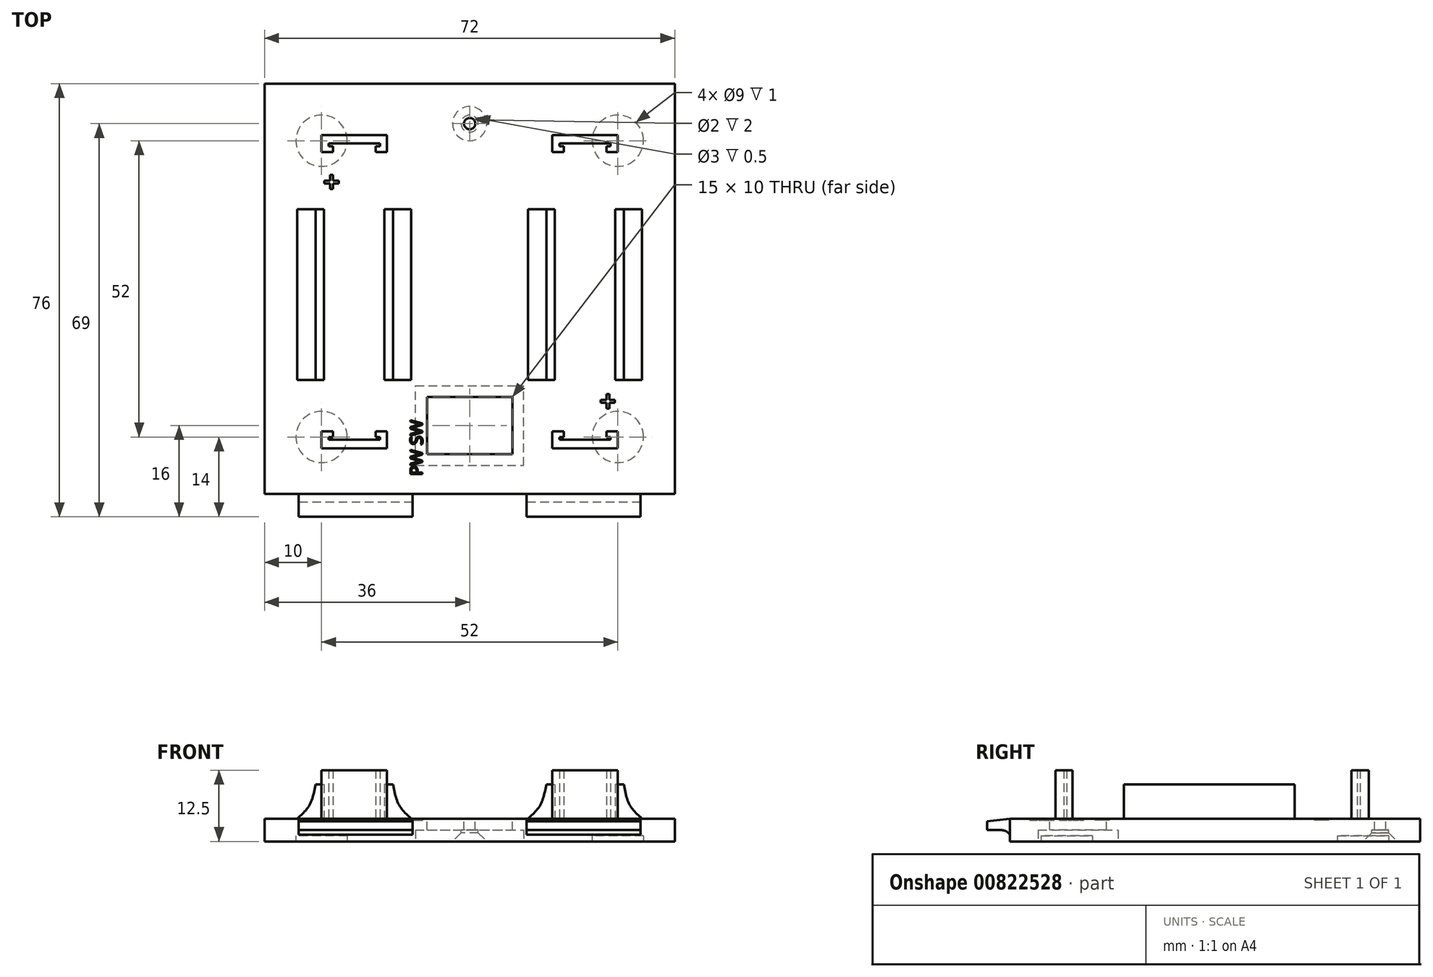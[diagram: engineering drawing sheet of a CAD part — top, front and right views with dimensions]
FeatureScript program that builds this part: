
annotation { "Feature Type Name" : "Feature", "Feature Type Description" : "" }
export const myFeature = defineFeature(function(context is Context, id is Id, definition is map)
    precondition{}
    {
        {
            var Q0;
            Q0=qCreatedBy(makeId("Top.planeOp"),FACE);
            var sketch = newSketch(context, id + "F0", { "sketchPlane" : qUnion([Q0])});
            skLineSegment(sketch, "E0.bottom", {"start": v(-36, 36) * mm, "end": v(36, 36) * mm});
            skLineSegment(sketch, "E0.top", {"start": v(-36, -36) * mm, "end": v(36, -36) * mm});
            skLineSegment(sketch, "E0.left", {"start": v(-36, 36) * mm, "end": v(-36, -36) * mm});
            skLineSegment(sketch, "E0.right", {"start": v(36, 36) * mm, "end": v(36, -36) * mm});
            skLineSegment(sketch, "E1.bottom", {"start": v(-36, -36) * mm, "end": v(-16, -36) * mm});
            skLineSegment(sketch, "E1.top", {"start": v(-36, -40) * mm, "end": v(-16, -40) * mm});
            skLineSegment(sketch, "E1.left", {"start": v(-36, -36) * mm, "end": v(-36, -40) * mm});
            skLineSegment(sketch, "E1.right", {"start": v(-16, -36) * mm, "end": v(-16, -40) * mm});
            skLineSegment(sketch, "E2.bottom", {"start": v(16, -36) * mm, "end": v(36, -36) * mm});
            skLineSegment(sketch, "E2.top", {"start": v(16, -40) * mm, "end": v(36, -40) * mm});
            skLineSegment(sketch, "E2.left", {"start": v(16, -36) * mm, "end": v(16, -40) * mm});
            skLineSegment(sketch, "E2.right", {"start": v(36, -36) * mm, "end": v(36, -40) * mm});
            skLineSegment(sketch, "E3", {"start": v(-16, -40) * mm, "end": v(16, -40) * mm});
            skLineSegment(sketch, "E4", {"start": v(-16, -36) * mm, "end": v(16, -36) * mm});
            skLineSegment(sketch, "E5", {"start": v(-10, -40) * mm, "end": v(-10, -36) * mm});
            skLineSegment(sketch, "E6", {"start": v(10, -40) * mm, "end": v(10, -36) * mm});
            skPoint(sketch, "E6.endSnap0", {"position": v(0, -36) * mm});
            skSolve(sketch);
        }
        {
            var Q0;
            Q0=makeQuery(id+"F0.imprint","IMPRINT",FACE,{"disambiguationData":[TD([[makeQuery(id+"F0.imprint","IMPRINT",EDGE,{"derivedFrom":sQuery(id+"F0.wireOp",EDGE,"E0.bottom")}),-1.0]])]});
            extrude(context, id + "F1", {"entities" : qUnion([Q0]), "depth" : 4 * mm, "offsetDistance" : 25 * mm});
        }
        {
            var Q0;
            Q0=makeQuery(id+"F1.opExtrude","CAP_FACE",FACE,{"disambiguationData":[OSD([sQuery(id+"F0.wireOp",EDGE,"E0.bottom"),sQuery(id+"F0.wireOp",EDGE,"E0.top"),sQuery(id+"F0.wireOp",EDGE,"E0.left"),sQuery(id+"F0.wireOp",EDGE,"E0.right")])],"isStart":false});
            var sketch = newSketch(context, id + "F2", { "sketchPlane" : qUnion([Q0])});
            skLineSegment(sketch, "E7.bottom", {"start": v(-26, 27) * mm, "end": v(-24, 27) * mm});
            skLineSegment(sketch, "E7.top", {"start": v(-26, 24) * mm, "end": v(-24, 24) * mm});
            skLineSegment(sketch, "E7.left", {"start": v(-26, 27) * mm, "end": v(-26, 24) * mm});
            skLineSegment(sketch, "E7.right", {"start": v(-24, 27) * mm, "end": v(-24, 24) * mm});
            skLineSegment(sketch, "E8.bottom", {"start": v(-16.5, 27) * mm, "end": v(-14.5, 27) * mm});
            skLineSegment(sketch, "E8.top", {"start": v(-16.5, 24) * mm, "end": v(-14.5, 24) * mm});
            skLineSegment(sketch, "E8.left", {"start": v(-16.5, 27) * mm, "end": v(-16.5, 24) * mm});
            skLineSegment(sketch, "E8.right", {"start": v(-14.5, 27) * mm, "end": v(-14.5, 24) * mm});
            skLineSegment(sketch, "E9", {"start": v(-24, 27) * mm, "end": v(-16.5, 27) * mm});
            skLineSegment(sketch, "E10", {"start": v(-24, 25) * mm, "end": v(-16.5, 25) * mm, "construction": true});
            skLineSegment(sketch, "E11", {"start": v(-24, 25.5) * mm, "end": v(-16.5, 25.5) * mm});
            skLineSegment(sketch, "E12", {"start": v(-24, 25.5) * mm, "end": v(-24.75, 25.5) * mm});
            skLineSegment(sketch, "E13", {"start": v(-24.75, 25.5) * mm, "end": v(-24.75, 25) * mm});
            skLineSegment(sketch, "E14", {"start": v(-24.75, 25) * mm, "end": v(-24, 25) * mm});
            skLineSegment(sketch, "E15", {"start": v(-16.5, 25.5) * mm, "end": v(-15.75, 25.5) * mm});
            skLineSegment(sketch, "E16", {"start": v(-15.75, 25.5) * mm, "end": v(-15.75, 25) * mm});
            skLineSegment(sketch, "E17", {"start": v(-15.75, 25) * mm, "end": v(-16.5, 25) * mm});
            skLineSegment(sketch, "E18.bottom", {"start": v(-14.5, -28) * mm, "end": v(-16.5, -28) * mm});
            skLineSegment(sketch, "E18.top", {"start": v(-14.5, -25) * mm, "end": v(-16.5, -25) * mm});
            skLineSegment(sketch, "E18.left", {"start": v(-14.5, -28) * mm, "end": v(-14.5, -25) * mm});
            skLineSegment(sketch, "E18.right", {"start": v(-16.5, -28) * mm, "end": v(-16.5, -25) * mm});
            skLineSegment(sketch, "E19.bottom", {"start": v(-24, -28) * mm, "end": v(-26, -28) * mm});
            skLineSegment(sketch, "E19.top", {"start": v(-24, -25) * mm, "end": v(-26, -25) * mm});
            skLineSegment(sketch, "E19.left", {"start": v(-24, -28) * mm, "end": v(-24, -25) * mm});
            skLineSegment(sketch, "E19.right", {"start": v(-26, -28) * mm, "end": v(-26, -25) * mm});
            skLineSegment(sketch, "E20", {"start": v(-16.5, -28) * mm, "end": v(-24, -28) * mm});
            skLineSegment(sketch, "E21", {"start": v(-16.5, -26) * mm, "end": v(-24, -26) * mm, "construction": true});
            skLineSegment(sketch, "E22", {"start": v(-16.5, -26.5) * mm, "end": v(-24, -26.5) * mm});
            skLineSegment(sketch, "E23", {"start": v(-16.5, -26.5) * mm, "end": v(-15.75, -26.5) * mm});
            skLineSegment(sketch, "E24", {"start": v(-15.75, -26.5) * mm, "end": v(-15.75, -26) * mm});
            skLineSegment(sketch, "E25", {"start": v(-15.75, -26) * mm, "end": v(-16.5, -26) * mm});
            skLineSegment(sketch, "E26", {"start": v(-24, -26.5) * mm, "end": v(-24.75, -26.5) * mm});
            skLineSegment(sketch, "E27", {"start": v(-24.75, -26.5) * mm, "end": v(-24.75, -26) * mm});
            skLineSegment(sketch, "E28", {"start": v(-24.75, -26) * mm, "end": v(-24, -26) * mm});
            skLineSegment(sketch, "E29.bottom", {"start": v(14.5, 27) * mm, "end": v(16.5, 27) * mm});
            skLineSegment(sketch, "E29.top", {"start": v(14.5, 24) * mm, "end": v(16.5, 24) * mm});
            skLineSegment(sketch, "E29.left", {"start": v(14.5, 27) * mm, "end": v(14.5, 24) * mm});
            skLineSegment(sketch, "E29.right", {"start": v(16.5, 27) * mm, "end": v(16.5, 24) * mm});
            skLineSegment(sketch, "E30.bottom", {"start": v(24, 27) * mm, "end": v(26, 27) * mm});
            skLineSegment(sketch, "E30.top", {"start": v(24, 24) * mm, "end": v(26, 24) * mm});
            skLineSegment(sketch, "E30.left", {"start": v(24, 27) * mm, "end": v(24, 24) * mm});
            skLineSegment(sketch, "E30.right", {"start": v(26, 27) * mm, "end": v(26, 24) * mm});
            skLineSegment(sketch, "E31", {"start": v(16.5, 27) * mm, "end": v(24, 27) * mm});
            skLineSegment(sketch, "E32", {"start": v(16.5, 25) * mm, "end": v(24, 25) * mm, "construction": true});
            skLineSegment(sketch, "E33", {"start": v(16.5, 25.5) * mm, "end": v(24, 25.5) * mm});
            skLineSegment(sketch, "E34", {"start": v(16.5, 25.5) * mm, "end": v(15.75, 25.5) * mm});
            skLineSegment(sketch, "E35", {"start": v(15.75, 25.5) * mm, "end": v(15.75, 25) * mm});
            skLineSegment(sketch, "E36", {"start": v(15.75, 25) * mm, "end": v(16.5, 25) * mm});
            skLineSegment(sketch, "E37", {"start": v(24, 25.5) * mm, "end": v(24.75, 25.5) * mm});
            skLineSegment(sketch, "E38", {"start": v(24.75, 25.5) * mm, "end": v(24.75, 25) * mm});
            skLineSegment(sketch, "E39", {"start": v(24.75, 25) * mm, "end": v(24, 25) * mm});
            skLineSegment(sketch, "E40.bottom", {"start": v(26, -28) * mm, "end": v(24, -28) * mm});
            skLineSegment(sketch, "E40.top", {"start": v(26, -25) * mm, "end": v(24, -25) * mm});
            skLineSegment(sketch, "E40.left", {"start": v(26, -28) * mm, "end": v(26, -25) * mm});
            skLineSegment(sketch, "E40.right", {"start": v(24, -28) * mm, "end": v(24, -25) * mm});
            skLineSegment(sketch, "E41.bottom", {"start": v(16.5, -28) * mm, "end": v(14.5, -28) * mm});
            skLineSegment(sketch, "E41.top", {"start": v(16.5, -25) * mm, "end": v(14.5, -25) * mm});
            skLineSegment(sketch, "E41.left", {"start": v(16.5, -28) * mm, "end": v(16.5, -25) * mm});
            skLineSegment(sketch, "E41.right", {"start": v(14.5, -28) * mm, "end": v(14.5, -25) * mm});
            skLineSegment(sketch, "E42", {"start": v(24, -28) * mm, "end": v(16.5, -28) * mm});
            skLineSegment(sketch, "E43", {"start": v(24, -26) * mm, "end": v(16.5, -26) * mm, "construction": true});
            skLineSegment(sketch, "E44", {"start": v(24, -26.5) * mm, "end": v(16.5, -26.5) * mm});
            skLineSegment(sketch, "E45", {"start": v(24, -26.5) * mm, "end": v(24.75, -26.5) * mm});
            skLineSegment(sketch, "E46", {"start": v(24.75, -26.5) * mm, "end": v(24.75, -26) * mm});
            skLineSegment(sketch, "E47", {"start": v(24.75, -26) * mm, "end": v(24, -26) * mm});
            skLineSegment(sketch, "E48", {"start": v(16.5, -26.5) * mm, "end": v(15.75, -26.5) * mm});
            skLineSegment(sketch, "E49", {"start": v(15.75, -26.5) * mm, "end": v(15.75, -26) * mm});
            skLineSegment(sketch, "E50", {"start": v(15.75, -26) * mm, "end": v(16.5, -26) * mm});
            skLineSegment(sketch, "E51", {"start": v(-14.5, 27) * mm, "end": v(14.5, 27) * mm, "construction": true});
            skLineSegment(sketch, "E52", {"start": v(-20.25, 25) * mm, "end": v(-20.25, -26) * mm, "construction": true});
            skLineSegment(sketch, "E53", {"start": v(20.25, 25) * mm, "end": v(20.25, -26) * mm, "construction": true});
            skLineSegment(sketch, "E54.bottom", {"start": v(-27.05, 14) * mm, "end": v(-25.55, 14) * mm});
            skLineSegment(sketch, "E54.top", {"start": v(-27.05, 4) * mm, "end": v(-25.55, 4) * mm});
            skLineSegment(sketch, "E54.left", {"start": v(-27.05, 14) * mm, "end": v(-27.05, 4) * mm});
            skLineSegment(sketch, "E54.right", {"start": v(-25.55, 14) * mm, "end": v(-25.55, 4) * mm});
            skLineSegment(sketch, "E55", {"start": v(-26, 24) * mm, "end": v(-42.81, 24) * mm, "construction": true});
            skLineSegment(sketch, "E56.bottom", {"start": v(-27.05, -6) * mm, "end": v(-25.55, -6) * mm});
            skLineSegment(sketch, "E56.top", {"start": v(-27.05, -16) * mm, "end": v(-25.55, -16) * mm});
            skLineSegment(sketch, "E56.left", {"start": v(-27.05, -6) * mm, "end": v(-27.05, -16) * mm});
            skLineSegment(sketch, "E56.right", {"start": v(-25.55, -6) * mm, "end": v(-25.55, -16) * mm});
            skLineSegment(sketch, "E57.MirrorCS", {"start": v(-14.95, 14) * mm, "end": v(-14.95, 4) * mm});
            skLineSegment(sketch, "E58.MirrorCS", {"start": v(-13.45, 14) * mm, "end": v(-13.45, 4) * mm});
            skLineSegment(sketch, "E59.MirrorCS", {"start": v(-13.45, 14) * mm, "end": v(-14.95, 14) * mm});
            skLineSegment(sketch, "E60.MirrorCS", {"start": v(-13.45, 4) * mm, "end": v(-14.95, 4) * mm});
            skLineSegment(sketch, "E61.MirrorCS", {"start": v(-14.95, -6) * mm, "end": v(-14.95, -16) * mm});
            skLineSegment(sketch, "E62.MirrorCS", {"start": v(-13.45, -6) * mm, "end": v(-13.45, -16) * mm});
            skLineSegment(sketch, "E63.MirrorCS", {"start": v(-13.45, -6) * mm, "end": v(-14.95, -6) * mm});
            skLineSegment(sketch, "E64.MirrorCS", {"start": v(-13.45, -16) * mm, "end": v(-14.95, -16) * mm});
            skLineSegment(sketch, "E65", {"start": v(14.5, 24) * mm, "end": v(3.37, 24) * mm, "construction": true});
            skLineSegment(sketch, "E66.bottom", {"start": v(13.45, 14) * mm, "end": v(14.95, 14) * mm});
            skLineSegment(sketch, "E66.top", {"start": v(13.45, 4) * mm, "end": v(14.95, 4) * mm});
            skLineSegment(sketch, "E66.left", {"start": v(13.45, 14) * mm, "end": v(13.45, 4) * mm});
            skLineSegment(sketch, "E66.right", {"start": v(14.95, 14) * mm, "end": v(14.95, 4) * mm});
            skLineSegment(sketch, "E67.bottom", {"start": v(13.45, -6) * mm, "end": v(14.95, -6) * mm});
            skLineSegment(sketch, "E67.top", {"start": v(13.45, -16) * mm, "end": v(14.95, -16) * mm});
            skLineSegment(sketch, "E67.left", {"start": v(13.45, -6) * mm, "end": v(13.45, -16) * mm});
            skLineSegment(sketch, "E67.right", {"start": v(14.95, -6) * mm, "end": v(14.95, -16) * mm});
            skLineSegment(sketch, "E68.MirrorCS", {"start": v(25.55, 14) * mm, "end": v(25.55, 4) * mm});
            skLineSegment(sketch, "E69.MirrorCS", {"start": v(27.05, 14) * mm, "end": v(27.05, 4) * mm});
            skLineSegment(sketch, "E70.MirrorCS", {"start": v(27.05, 4) * mm, "end": v(25.55, 4) * mm});
            skLineSegment(sketch, "E71.MirrorCS", {"start": v(27.05, 14) * mm, "end": v(25.55, 14) * mm});
            skLineSegment(sketch, "E72.MirrorCS", {"start": v(27.05, -6) * mm, "end": v(25.55, -6) * mm});
            skLineSegment(sketch, "E73.MirrorCS", {"start": v(25.55, -6) * mm, "end": v(25.55, -16) * mm});
            skLineSegment(sketch, "E74.MirrorCS", {"start": v(27.05, -6) * mm, "end": v(27.05, -16) * mm});
            skLineSegment(sketch, "E75.MirrorCS", {"start": v(27.05, -16) * mm, "end": v(25.55, -16) * mm});
            skLineSegment(sketch, "E76", {"start": v(-24, -25) * mm, "end": v(-16.5, -25) * mm, "construction": true});
            skLineSegment(sketch, "E77", {"start": v(16.5, -25) * mm, "end": v(24, -25) * mm, "construction": true});
            skLineSegment(sketch, "E78", {"start": v(16.5, 24) * mm, "end": v(24, 24) * mm, "construction": true});
            skLineSegment(sketch, "E79", {"start": v(-24, 24) * mm, "end": v(-16.5, 24) * mm, "construction": true});
            skLineSegment(sketch, "E80.bottom", {"start": v(-24.5, 20) * mm, "end": v(-24, 20) * mm});
            skLineSegment(sketch, "E80.top", {"start": v(-24.5, 17.5) * mm, "end": v(-24, 17.5) * mm});
            skLineSegment(sketch, "E80.left", {"start": v(-24.5, 20) * mm, "end": v(-24.5, 19) * mm});
            skLineSegment(sketch, "E80.right", {"start": v(-24, 20) * mm, "end": v(-24, 19) * mm});
            skLineSegment(sketch, "E81.bottom", {"start": v(-23, 19) * mm, "end": v(-24, 19) * mm});
            skLineSegment(sketch, "E81.top", {"start": v(-23, 18.5) * mm, "end": v(-24, 18.5) * mm});
            skLineSegment(sketch, "E81.left", {"start": v(-23, 19) * mm, "end": v(-23, 18.5) * mm});
            skLineSegment(sketch, "E81.right", {"start": v(-25.5, 19) * mm, "end": v(-25.5, 18.5) * mm});
            skLineSegment(sketch, "E82", {"start": v(-25.5, 18.75) * mm, "end": v(-23, 18.75) * mm, "construction": true});
            skLineSegment(sketch, "E83", {"start": v(-24.25, 20) * mm, "end": v(-24.25, 17.5) * mm, "construction": true});
            skLineSegment(sketch, "E84.trimOffspring", {"start": v(-24.5, 18.5) * mm, "end": v(-24.5, 17.5) * mm});
            skLineSegment(sketch, "E85.trimOffspring", {"start": v(-24.5, 18.5) * mm, "end": v(-25.5, 18.5) * mm});
            skLineSegment(sketch, "E86.trimOffspring", {"start": v(-24, 18.5) * mm, "end": v(-24, 17.5) * mm});
            skLineSegment(sketch, "E87.trimOffspring", {"start": v(-24.5, 19) * mm, "end": v(-25.5, 19) * mm});
            skLineSegment(sketch, "E88.bottom", {"start": v(24, -18.5) * mm, "end": v(24.5, -18.5) * mm});
            skLineSegment(sketch, "E88.top", {"start": v(24, -21) * mm, "end": v(24.5, -21) * mm});
            skLineSegment(sketch, "E88.left", {"start": v(24, -18.5) * mm, "end": v(24, -19.5) * mm});
            skLineSegment(sketch, "E88.right", {"start": v(24.5, -18.5) * mm, "end": v(24.5, -19.5) * mm});
            skLineSegment(sketch, "E89.bottom", {"start": v(25.5, -19.5) * mm, "end": v(24.5, -19.5) * mm});
            skLineSegment(sketch, "E89.top", {"start": v(25.5, -20) * mm, "end": v(24.5, -20) * mm});
            skLineSegment(sketch, "E89.left", {"start": v(25.5, -19.5) * mm, "end": v(25.5, -20) * mm});
            skLineSegment(sketch, "E89.right", {"start": v(23, -19.5) * mm, "end": v(23, -20) * mm});
            skLineSegment(sketch, "E90", {"start": v(23, -19.75) * mm, "end": v(25.5, -19.75) * mm, "construction": true});
            skLineSegment(sketch, "E91", {"start": v(24.25, -18.5) * mm, "end": v(24.25, -21) * mm, "construction": true});
            skLineSegment(sketch, "E92.trimOffspring", {"start": v(24, -20) * mm, "end": v(24, -21) * mm});
            skLineSegment(sketch, "E93.trimOffspring", {"start": v(24, -20) * mm, "end": v(23, -20) * mm});
            skLineSegment(sketch, "E94.trimOffspring", {"start": v(24.5, -20) * mm, "end": v(24.5, -21) * mm});
            skLineSegment(sketch, "E95.trimOffspring", {"start": v(24, -19.5) * mm, "end": v(23, -19.5) * mm});
            skLineSegment(sketch, "E96", {"start": v(-27.05, 4) * mm, "end": v(-27.05, -6) * mm});
            skLineSegment(sketch, "E97", {"start": v(-25.55, 4) * mm, "end": v(-25.55, -6) * mm});
            skLineSegment(sketch, "E98", {"start": v(-14.95, 4) * mm, "end": v(-14.95, -6) * mm});
            skLineSegment(sketch, "E99", {"start": v(-13.45, 4) * mm, "end": v(-13.45, -6) * mm});
            skLineSegment(sketch, "E100", {"start": v(25.55, 4) * mm, "end": v(25.55, -6) * mm});
            skLineSegment(sketch, "E101", {"start": v(27.05, 4) * mm, "end": v(27.05, -6) * mm});
            skLineSegment(sketch, "E102", {"start": v(13.45, 4) * mm, "end": v(13.45, -6) * mm});
            skLineSegment(sketch, "E103", {"start": v(14.95, 4) * mm, "end": v(14.95, -6) * mm});
            skSolve(sketch);
        }
        {
            var Q0;
            Q0=makeQuery(id+"F2.imprint","IMPRINT",FACE,{"disambiguationData":[TD([[makeQuery(id+"F2.imprint","IMPRINT",EDGE,{"derivedFrom":sQuery(id+"F2.wireOp",EDGE,"E56.bottom")}),-1.0]])]});
            var Q1;
            Q1=makeQuery(id+"F2.imprint","IMPRINT",FACE,{"disambiguationData":[TD([[makeQuery(id+"F2.imprint","IMPRINT",EDGE,{"derivedFrom":sQuery(id+"F2.wireOp",EDGE,"E61.MirrorCS")}),1.0]])]});
            var Q2;
            Q2=makeQuery(id+"F2.imprint","IMPRINT",FACE,{"disambiguationData":[TD([[makeQuery(id+"F2.imprint","IMPRINT",EDGE,{"derivedFrom":sQuery(id+"F2.wireOp",EDGE,"E57.MirrorCS")}),1.0]])]});
            var Q3;
            Q3=makeQuery(id+"F2.imprint","IMPRINT",FACE,{"disambiguationData":[TD([[makeQuery(id+"F2.imprint","IMPRINT",EDGE,{"derivedFrom":sQuery(id+"F2.wireOp",EDGE,"E54.bottom")}),-1.0]])]});
            var Q4;
            Q4=makeQuery(id+"F2.imprint","IMPRINT",FACE,{"disambiguationData":[TD([[makeQuery(id+"F2.imprint","IMPRINT",EDGE,{"derivedFrom":sQuery(id+"F2.wireOp",EDGE,"E67.bottom")}),-1.0]])]});
            var Q5;
            Q5=makeQuery(id+"F2.imprint","IMPRINT",FACE,{"disambiguationData":[TD([[makeQuery(id+"F2.imprint","IMPRINT",EDGE,{"derivedFrom":sQuery(id+"F2.wireOp",EDGE,"E66.bottom")}),-1.0]])]});
            var Q6;
            Q6=makeQuery(id+"F2.imprint","IMPRINT",FACE,{"disambiguationData":[TD([[makeQuery(id+"F2.imprint","IMPRINT",EDGE,{"derivedFrom":sQuery(id+"F2.wireOp",EDGE,"E68.MirrorCS")}),1.0]])]});
            var Q7;
            Q7=makeQuery(id+"F2.imprint","IMPRINT",FACE,{"disambiguationData":[TD([[makeQuery(id+"F2.imprint","IMPRINT",EDGE,{"derivedFrom":sQuery(id+"F2.wireOp",EDGE,"E72.MirrorCS")}),1.0]])]});
            var Q8;
            Q8=makeQuery(id+"F2.imprint","IMPRINT",FACE,{"disambiguationData":[TD([[makeQuery(id+"F2.imprint","IMPRINT",EDGE,{"derivedFrom":sQuery(id+"F2.wireOp",EDGE,"E54.top")}),-1.0]])]});
            var Q9;
            Q9=makeQuery(id+"F2.imprint","IMPRINT",FACE,{"disambiguationData":[TD([[makeQuery(id+"F2.imprint","IMPRINT",EDGE,{"derivedFrom":sQuery(id+"F2.wireOp",EDGE,"E60.MirrorCS")}),1.0]])]});
            var Q10;
            Q10=makeQuery(id+"F2.imprint","IMPRINT",FACE,{"disambiguationData":[TD([[makeQuery(id+"F2.imprint","IMPRINT",EDGE,{"derivedFrom":sQuery(id+"F2.wireOp",EDGE,"E66.top")}),-1.0]])]});
            var Q11;
            Q11=makeQuery(id+"F2.imprint","IMPRINT",FACE,{"disambiguationData":[TD([[makeQuery(id+"F2.imprint","IMPRINT",EDGE,{"derivedFrom":sQuery(id+"F2.wireOp",EDGE,"E70.MirrorCS")}),1.0]])]});
            extrude(context, id + "F3", {"entities" : qUnion([Q0, Q1, Q2, Q3, Q4, Q5, Q6, Q7, Q8, Q9, Q10, Q11]), "operationType" : NewBodyOperationType.ADD, "depth" : 6 * mm, "offsetDistance" : 25 * mm});
        }
        {
            var Q0;
            {var subQ1=sQuery(id+"F2.wireOp",EDGE,"E7.bottom");Q0=makeQuery(id+"F2.imprint","IMPRINT",FACE,{"disambiguationData":[TD([[makeQuery(id+"F2.imprint","IMPRINT",EDGE,{"derivedFrom":subQ1}),-1.0]])]});}
            var Q1;
            {var subQ0=sQuery(id+"F2.wireOp",EDGE,"E9");Q1=makeQuery(id+"F2.imprint","IMPRINT",FACE,{"disambiguationData":[TD([[makeQuery(id+"F2.imprint","IMPRINT",EDGE,{"derivedFrom":subQ0}),-1.0]])]});}
            var Q2;
            {var subQ3=sQuery(id+"F2.wireOp",EDGE,"E8.bottom");Q2=makeQuery(id+"F2.imprint","IMPRINT",FACE,{"disambiguationData":[TD([[makeQuery(id+"F2.imprint","IMPRINT",EDGE,{"derivedFrom":subQ3}),-1.0]])]});}
            var Q3;
            {var subQ1=sQuery(id+"F2.wireOp",EDGE,"E18.bottom");Q3=makeQuery(id+"F2.imprint","IMPRINT",FACE,{"disambiguationData":[TD([[makeQuery(id+"F2.imprint","IMPRINT",EDGE,{"derivedFrom":subQ1}),-1.0]])]});}
            var Q4;
            {var subQ0=sQuery(id+"F2.wireOp",EDGE,"E20");Q4=makeQuery(id+"F2.imprint","IMPRINT",FACE,{"disambiguationData":[TD([[makeQuery(id+"F2.imprint","IMPRINT",EDGE,{"derivedFrom":subQ0}),-1.0]])]});}
            var Q5;
            {var subQ3=sQuery(id+"F2.wireOp",EDGE,"E19.bottom");Q5=makeQuery(id+"F2.imprint","IMPRINT",FACE,{"disambiguationData":[TD([[makeQuery(id+"F2.imprint","IMPRINT",EDGE,{"derivedFrom":subQ3}),-1.0]])]});}
            var Q6;
            {var subQ1=sQuery(id+"F2.wireOp",EDGE,"E29.bottom");Q6=makeQuery(id+"F2.imprint","IMPRINT",FACE,{"disambiguationData":[TD([[makeQuery(id+"F2.imprint","IMPRINT",EDGE,{"derivedFrom":subQ1}),-1.0]])]});}
            var Q7;
            {var subQ0=sQuery(id+"F2.wireOp",EDGE,"E31");Q7=makeQuery(id+"F2.imprint","IMPRINT",FACE,{"disambiguationData":[TD([[makeQuery(id+"F2.imprint","IMPRINT",EDGE,{"derivedFrom":subQ0}),-1.0]])]});}
            var Q8;
            {var subQ3=sQuery(id+"F2.wireOp",EDGE,"E30.bottom");Q8=makeQuery(id+"F2.imprint","IMPRINT",FACE,{"disambiguationData":[TD([[makeQuery(id+"F2.imprint","IMPRINT",EDGE,{"derivedFrom":subQ3}),-1.0]])]});}
            var Q9;
            {var subQ1=sQuery(id+"F2.wireOp",EDGE,"E40.bottom");Q9=makeQuery(id+"F2.imprint","IMPRINT",FACE,{"disambiguationData":[TD([[makeQuery(id+"F2.imprint","IMPRINT",EDGE,{"derivedFrom":subQ1}),-1.0]])]});}
            var Q10;
            {var subQ0=sQuery(id+"F2.wireOp",EDGE,"E42");Q10=makeQuery(id+"F2.imprint","IMPRINT",FACE,{"disambiguationData":[TD([[makeQuery(id+"F2.imprint","IMPRINT",EDGE,{"derivedFrom":subQ0}),-1.0]])]});}
            var Q11;
            {var subQ3=sQuery(id+"F2.wireOp",EDGE,"E41.bottom");Q11=makeQuery(id+"F2.imprint","IMPRINT",FACE,{"disambiguationData":[TD([[makeQuery(id+"F2.imprint","IMPRINT",EDGE,{"derivedFrom":subQ3}),-1.0]])]});}
            extrude(context, id + "F4", {"entities" : qUnion([Q0, Q1, Q2, Q3, Q4, Q5, Q6, Q7, Q8, Q9, Q10, Q11]), "operationType" : NewBodyOperationType.ADD, "depth" : 8.5 * mm, "offsetDistance" : 25 * mm});
        }
        {
            var Q0;
            Q0=qCreatedBy(makeId("Front.planeOp"),FACE);
            var sketch = newSketch(context, id + "F5", { "sketchPlane" : qUnion([Q0])});
            skLineSegment(sketch, "E104.top", {"start": v(-30.24, 4) * mm, "end": v(-27.05, 4) * mm});
            skLineSegment(sketch, "E104.right", {"start": v(-27.05, 10) * mm, "end": v(-27.05, 4) * mm});
            skPoint(sketch, "E105", {"position": v(-30.24, 4) * mm});
            skFitSpline(sketch, "E106", {"points": [v(-27.05, 10) * mm, v(-28.1, 6.43) * mm, v(-30.24, 4) * mm], "startDerivative": vector(-1.38, -7.39) * mm, "endDerivative": vector(-5.04, -4.58) * mm});
            skLineSegment(sketch, "E107", {"start": v(-20.25, 13.7) * mm, "end": v(-20.25, 3.33) * mm, "construction": true});
            skFitSpline(sketch, "E108.MirrorCS", {"points": [v(-13.45, 10) * mm, v(-12.4, 6.43) * mm, v(-10.26, 4) * mm], "startDerivative": vector(1.38, -7.39) * mm, "endDerivative": vector(5.04, -4.58) * mm});
            skLineSegment(sketch, "E109", {"start": v(20.25, 13.97) * mm, "end": v(20.25, 2.5) * mm, "construction": true});
            skLineSegment(sketch, "E110.MirrorCS", {"start": v(-13.45, 10) * mm, "end": v(-13.45, 4) * mm});
            skLineSegment(sketch, "E111.MirrorCS", {"start": v(-10.26, 4) * mm, "end": v(-13.45, 4) * mm});
            skFitSpline(sketch, "E112.MirrorCS", {"points": [v(13.45, 10) * mm, v(12.4, 6.43) * mm, v(10.26, 4) * mm], "startDerivative": vector(-1.38, -7.39) * mm, "endDerivative": vector(-5.04, -4.58) * mm});
            skFitSpline(sketch, "E113.MirrorCS", {"points": [v(27.05, 10) * mm, v(28.1, 6.43) * mm, v(30.24, 4) * mm], "startDerivative": vector(1.38, -7.39) * mm, "endDerivative": vector(5.04, -4.58) * mm});
            skLineSegment(sketch, "E114.MirrorCS", {"start": v(30.24, 4) * mm, "end": v(27.05, 4) * mm});
            skLineSegment(sketch, "E115.MirrorCS", {"start": v(27.05, 10) * mm, "end": v(27.05, 4) * mm});
            skLineSegment(sketch, "E116.MirrorCS", {"start": v(13.45, 10) * mm, "end": v(13.45, 4) * mm});
            skLineSegment(sketch, "E117.MirrorCS", {"start": v(10.26, 4) * mm, "end": v(13.45, 4) * mm});
            skSolve(sketch);
        }
        {
            var Q0;
            Q0=makeQuery(id+"F1.opExtrude","CAP_FACE",FACE,{"disambiguationData":[OSD([sQuery(id+"F0.wireOp",EDGE,"E0.bottom"),sQuery(id+"F0.wireOp",EDGE,"E0.top"),sQuery(id+"F0.wireOp",EDGE,"E0.left"),sQuery(id+"F0.wireOp",EDGE,"E0.right")])],"isStart":false});
            var sketch = newSketch(context, id + "F6", { "sketchPlane" : qUnion([Q0])});
            skCircle(sketch, "E118", {"center": v(0, 29) * mm, "radius": 1.5 * mm});
            skCircle(sketch, "E119", {"center": v(0, 29) * mm, "radius": 1 * mm});
            skSolve(sketch);
        }
        {
            var Q0;
            Q0=makeQuery(id+"F6.imprint","IMPRINT",FACE,{"disambiguationData":[TD([[makeQuery(id+"F6.imprint","IMPRINT",EDGE,{"derivedFrom":sQuery(id+"F6.wireOp",EDGE,"E119")}),1.0]])]});
            extrude(context, id + "F7", {"entities" : qUnion([Q0]), "operationType" : NewBodyOperationType.REMOVE, "oppositeDirection" : true, "depth" : 25 * mm, "offsetDistance" : 25 * mm});
        }
        {
            var Q0;
            Q0=makeQuery(id+"F6.imprint","IMPRINT",FACE,{"disambiguationData":[TD([[makeQuery(id+"F6.imprint","IMPRINT",EDGE,{"derivedFrom":sQuery(id+"F6.wireOp",EDGE,"E118")}),1.0]])]});
            extrude(context, id + "F8", {"entities" : qUnion([Q0]), "operationType" : NewBodyOperationType.REMOVE, "oppositeDirection" : true, "depth" : 25 * mm, "offsetDistance" : 25 * mm, "hasSecondDirection" : true, "secondDirectionOppositeDirection" : true, "secondDirectionDepth" : 2 * mm});
        }
        {
            var Q0;
            Q0=makeQuery(id+"F8.boolean.opBoolean","INTERSECT",EDGE,{"derivedFrom":[makeQuery(id+"F1.opExtrude","CAP_FACE",FACE,{"disambiguationData":[OSD([sQuery(id+"F0.wireOp",EDGE,"E0.bottom"),sQuery(id+"F0.wireOp",EDGE,"E0.top"),sQuery(id+"F0.wireOp",EDGE,"E0.left"),sQuery(id+"F0.wireOp",EDGE,"E0.right")])],"isStart":true}),makeQuery(id+"F8.opExtrude","SWEPT_FACE",FACE,{"disambiguationData":[OSD([sQuery(id+"F6.wireOp",EDGE,"E118")])]})]});
            chamfer(context, id + "F9", {"entities" : qUnion([Q0]), "width" : 1.5 * mm, "tangentPropagation" : true});
        }
        {
            var Q0;
            Q0=qCreatedBy(makeId("Right.planeOp"),FACE);
            var sketch = newSketch(context, id + "F10", { "sketchPlane" : qUnion([Q0])});
            skLineSegment(sketch, "E120", {"start": v(-40, 2) * mm, "end": v(-36, 2) * mm});
            skLineSegment(sketch, "E121", {"start": v(-40, 3.5) * mm, "end": v(-40, 2) * mm});
            skLineSegment(sketch, "E122", {"start": v(-36, 2) * mm, "end": v(-36, 4) * mm});
            skLineSegment(sketch, "E123", {"start": v(-36, 2) * mm, "end": v(-36, 1.17) * mm});
            skFitSpline(sketch, "E124", {"points": [v(-36, 1.17) * mm, v(-36.47, 1.69) * mm, v(-37.49, 2) * mm], "startDerivative": vector(-0.7, 1.17) * mm, "endDerivative": vector(-2.73, 0.54) * mm});
            skLineSegment(sketch, "E125", {"start": v(-40, 3.5) * mm, "end": v(-36, 4) * mm});
            skPoint(sketch, "E126.orphan", {"position": v(-40, 4) * mm});
            skSolve(sketch);
        }
        {
            var Q0;
            {var subQ4=sQuery(id+"F10.wireOp",EDGE,"E122");Q0=makeQuery(id+"F10.imprint","IMPRINT",FACE,{"disambiguationData":[TD([[makeQuery(id+"F10.imprint","IMPRINT",EDGE,{"derivedFrom":subQ4}),1.0]])]});}
            var Q1;
            {var subQ3=sQuery(id+"F10.wireOp",EDGE,"E124");Q1=makeQuery(id+"F10.imprint","IMPRINT",FACE,{"disambiguationData":[TD([[makeQuery(id+"F10.imprint","IMPRINT",EDGE,{"derivedFrom":subQ3}),-1.0]])]});}
            extrude(context, id + "F11", {"entities" : qUnion([Q0, Q1]), "operationType" : NewBodyOperationType.ADD, "depth" : 30 * mm, "offsetDistance" : 25 * mm, "hasSecondDirection" : true, "secondDirectionOppositeDirection" : true, "secondDirectionDepth" : 30 * mm});
        }
        {
            var Q0;
            Q0=makeQuery(id+"F0.imprint","IMPRINT",FACE,{"disambiguationData":[TD([[makeQuery(id+"F0.imprint","IMPRINT",EDGE,{"derivedFrom":sQuery(id+"F0.wireOp",EDGE,"E1.bottom")}),-1.0]])]});
            var Q1;
            {var subQ0=sQuery(id+"F0.wireOp",EDGE,"E5");Q1=makeQuery(id+"F0.imprint","IMPRINT",FACE,{"disambiguationData":[TD([[makeQuery(id+"F0.imprint","IMPRINT",EDGE,{"derivedFrom":subQ0}),-1.0]])]});}
            var Q2;
            Q2=makeQuery(id+"F0.imprint","IMPRINT",FACE,{"disambiguationData":[TD([[makeQuery(id+"F0.imprint","IMPRINT",EDGE,{"derivedFrom":sQuery(id+"F0.wireOp",EDGE,"E2.bottom")}),-1.0]])]});
            extrude(context, id + "F12", {"entities" : qUnion([Q0, Q1, Q2]), "operationType" : NewBodyOperationType.REMOVE, "depth" : 18.6 * mm, "offsetDistance" : 25 * mm});
        }
        {
            var Q0;
            Q0=makeQuery(id+"F2.imprint","IMPRINT",FACE,{"disambiguationData":[TD([[makeQuery(id+"F2.imprint","IMPRINT",EDGE,{"derivedFrom":sQuery(id+"F2.wireOp",EDGE,"E80.bottom")}),-1.0]])]});
            var Q1;
            Q1=makeQuery(id+"F2.imprint","IMPRINT",FACE,{"disambiguationData":[TD([[makeQuery(id+"F2.imprint","IMPRINT",EDGE,{"derivedFrom":sQuery(id+"F2.wireOp",EDGE,"E88.bottom")}),-1.0]])]});
            extrude(context, id + "F13", {"entities" : qUnion([Q0, Q1]), "operationType" : NewBodyOperationType.REMOVE, "oppositeDirection" : true, "depth" : .3 * mm, "offsetDistance" : 25 * mm});
        }
        {
            var Q0;
            Q0=makeQuery(id+"F6.imprint","IMPRINT",FACE,{"disambiguationData":[TD([[makeQuery(id+"F6.imprint","IMPRINT",EDGE,{"derivedFrom":sQuery(id+"F6.wireOp",EDGE,"E118")}),-1.0]])]});
            var sketch = newSketch(context, id + "F14", { "sketchPlane" : qUnion([Q0])});
            skLineSegment(sketch, "E127.bottom", {"start": v(-7.5, -19) * mm, "end": v(7.5, -19) * mm});
            skLineSegment(sketch, "E127.top", {"start": v(-7.5, -29) * mm, "end": v(7.5, -29) * mm});
            skLineSegment(sketch, "E127.left", {"start": v(-7.5, -19) * mm, "end": v(-7.5, -29) * mm});
            skLineSegment(sketch, "E127.right", {"start": v(7.5, -19) * mm, "end": v(7.5, -29) * mm});
            skPoint(sketch, "E128", {"position": v(0, -19) * mm});
            skSolve(sketch);
        }
        {
            var Q0;
            Q0=makeQuery(id+"F14.imprint","IMPRINT",FACE,{"disambiguationData":[TD([[makeQuery(id+"F14.imprint","IMPRINT",EDGE,{"derivedFrom":sQuery(id+"F14.wireOp",EDGE,"E127.bottom")}),-1.0]])]});
            extrude(context, id + "F15", {"entities" : qUnion([Q0]), "operationType" : NewBodyOperationType.REMOVE, "oppositeDirection" : true, "depth" : 25 * mm, "offsetDistance" : 25 * mm});
        }
        {
            var Q0;
            Q0=makeQuery(id+"F6.imprint","IMPRINT",FACE,{"disambiguationData":[TD([[makeQuery(id+"F6.imprint","IMPRINT",EDGE,{"derivedFrom":sQuery(id+"F6.wireOp",EDGE,"E118")}),-1.0]])]});
            var sketch = newSketch(context, id + "F16", { "sketchPlane" : qUnion([Q0])});
            skText(sketch, "E129", { "text": "PW SW\n", "fontName": "OpenSans-Regular.ttf"});
            const initialGuessF16  = {"E129": [-0.00828, -0.0328, 0, 1, 0.00216]};
            skSetInitialGuess(sketch, initialGuessF16);
            skSolve(sketch);
        }
        {
            var Q0;
            Q0=qSketchRegion(id+"F16",true);
            var Q1;
            Q1=qConstructionFilter(qBodyType(qCreatedBy(id+"F16",EDGE),BodyType.WIRE),ConstructionObject.NO);
            extrude(context, id + "F17", {"entities" : qUnion([Q0]), "operationType" : NewBodyOperationType.REMOVE, "surfaceOperationType" : NewSurfaceOperationType.ADD, "surfaceEntities" : qUnion([Q1]), "oppositeDirection" : true, "depth" : .3 * mm, "offsetDistance" : 25 * mm});
        }
        {
            var Q0;
            Q0=makeQuery(id+"F0.imprint","IMPRINT",FACE,{"disambiguationData":[TD([[makeQuery(id+"F0.imprint","IMPRINT",EDGE,{"derivedFrom":sQuery(id+"F0.wireOp",EDGE,"E0.bottom")}),-1.0]])]});
            var sketch = newSketch(context, id + "F18", { "sketchPlane" : qUnion([Q0])});
            skCircle(sketch, "E130", {"center": v(-26, -26) * mm, "radius": 7 * mm});
            skCircle(sketch, "E131", {"center": v(26, -26) * mm, "radius": 7 * mm});
            skCircle(sketch, "E132", {"center": v(-26, 26) * mm, "radius": 7 * mm});
            skCircle(sketch, "E133", {"center": v(26, 26) * mm, "radius": 7 * mm});
            skCircle(sketch, "E134", {"center": v(-26, -26) * mm, "radius": 4.5 * mm});
            skCircle(sketch, "E135", {"center": v(26, -26) * mm, "radius": 4.5 * mm});
            skCircle(sketch, "E136", {"center": v(-26, 26) * mm, "radius": 4.5 * mm});
            skCircle(sketch, "E137", {"center": v(26, 26) * mm, "radius": 4.5 * mm});
            skSolve(sketch);
        }
        {
            var Q0;
            Q0=makeQuery(id+"F18.imprint","IMPRINT",FACE,{"disambiguationData":[TD([[makeQuery(id+"F18.imprint","IMPRINT",EDGE,{"derivedFrom":sQuery(id+"F18.wireOp",EDGE,"E137")}),1.0]])]});
            var Q1;
            Q1=makeQuery(id+"F18.imprint","IMPRINT",FACE,{"disambiguationData":[TD([[makeQuery(id+"F18.imprint","IMPRINT",EDGE,{"derivedFrom":sQuery(id+"F18.wireOp",EDGE,"E136")}),1.0]])]});
            var Q2;
            Q2=makeQuery(id+"F18.imprint","IMPRINT",FACE,{"disambiguationData":[TD([[makeQuery(id+"F18.imprint","IMPRINT",EDGE,{"derivedFrom":sQuery(id+"F18.wireOp",EDGE,"E134")}),1.0]])]});
            var Q3;
            Q3=makeQuery(id+"F18.imprint","IMPRINT",FACE,{"disambiguationData":[TD([[makeQuery(id+"F18.imprint","IMPRINT",EDGE,{"derivedFrom":sQuery(id+"F18.wireOp",EDGE,"E135")}),1.0]])]});
            extrude(context, id + "F19", {"entities" : qUnion([Q0, Q1, Q2, Q3]), "operationType" : NewBodyOperationType.REMOVE, "oppositeDirection" : true, "depth" : -1 * mm, "offsetDistance" : 25 * mm});
        }
        {
            var Q0;
            Q0=makeQuery(id+"F1.opExtrude","CAP_FACE",FACE,{"disambiguationData":[OSD([sQuery(id+"F0.wireOp",EDGE,"E0.bottom"),sQuery(id+"F0.wireOp",EDGE,"E0.left"),sQuery(id+"F0.wireOp",EDGE,"E0.right"),sQuery(id+"F0.wireOp",EDGE,"E1.bottom"),sQuery(id+"F0.wireOp",EDGE,"E2.bottom"),sQuery(id+"F0.wireOp",EDGE,"E4")])],"isStart":true});
            var sketch = newSketch(context, id + "F20", { "sketchPlane" : qUnion([Q0])});
            skLineSegment(sketch, "E138.bottom", {"start": v(-9.5, 31) * mm, "end": v(9.5, 31) * mm});
            skLineSegment(sketch, "E138.top", {"start": v(-9.5, 17) * mm, "end": v(9.5, 17) * mm});
            skLineSegment(sketch, "E138.left", {"start": v(-9.5, 31) * mm, "end": v(-9.5, 17) * mm});
            skLineSegment(sketch, "E138.right", {"start": v(9.5, 31) * mm, "end": v(9.5, 17) * mm});
            skPoint(sketch, "E139", {"position": v(0, 31) * mm});
            skSolve(sketch);
        }
        {
            var Q0;
            Q0=qSketchRegion(id+"F20",true);
            extrude(context, id + "F21", {"entities" : qUnion([Q0]), "operationType" : NewBodyOperationType.REMOVE, "oppositeDirection" : true, "depth" : 2 * mm, "offsetDistance" : 25 * mm});
        }
        {
            var Q0;
            Q0=qSketchRegion(id+"F5",true);
            extrude(context, id + "F22", {"entities" : qUnion([Q0]), "operationType" : NewBodyOperationType.ADD, "depth" : 16 * mm, "offsetDistance" : 25 * mm, "hasSecondDirection" : true, "secondDirectionOppositeDirection" : true, "secondDirectionDepth" : 14 * mm});
        }
    });
